# Revit family: Ecowool Classic Board (80kgm3)
name_source: partatom
category: Generic Models
units: mm (PartAtom-declared; Revit-internal decimal feet)

## family parameters
Can host rebar = No
Cut with Voids When Loaded = No
Host = Face
Part Type = Normal
Room Calculation Point = No
Round Connector Dimension = Use Diameter
Shared = No

## types (2) — shared parameters
Default Elevation = 1219 mm
Density = 80.00 kg/m³
Finish = Classic Board
Manufacturer = PGF Insulation Sdn. Bhd.
Thermal K value = 0.0309
Type of Insulation = Glass Mineral Wool Insulation

## per-type parameters (varying)
| type | Description | Insulation Thickness | Thermal R value |
| EWBR 2580 (25mm) | ECOWOOL™ CLASSIC board is specifically designed to provide superior
fire resistance, acoustical and thermal insulation properties when
installed in glass, metal or in fabricated metal pans. ECOWOOL™, the
new generation of glass mineral wool has been engineered to provide
the highest levels of thermal and acoustic performance for building
occupants to achieve the level of indoor comfort deserved.
Made from almost 80% recycled glass and locally sourced raw
materials, ECOWOOL™ range of glass mineral wool is perfectly in tune
with sustainability and environmental concerns. | 25 mm  [stored 0.082021 ft] | 0.8 |
| EWBR 5080 (50mm) | ECOWOOL™ CLASSIC board is specifically designed to provide superior
fire resistance, acoustical and thermal insulation properties when
installed in glass, metal or in fabricated metal pans. ECOWOOL™, the
new generation of glass mineral wool has been engineered to provide
the highest levels of thermal and acoustic performance for building
occupants to achieve the level of indoor comfort deserved.
Made from almost 80% recycled glass and locally sourced raw
materials, ECOWOOL™ range of glass mineral wool is perfectly in tune
with sustainability and environmental concerns | 50 mm  [stored 0.164042 ft] | 1.6 |

note: [stored X ft] marks values corroborated as IEEE doubles in the binary element streams (Revit-internal decimal feet)

## geometry (parser evidence)
native form markers: Sweep x2
no freeform markers — native parametric forms only
